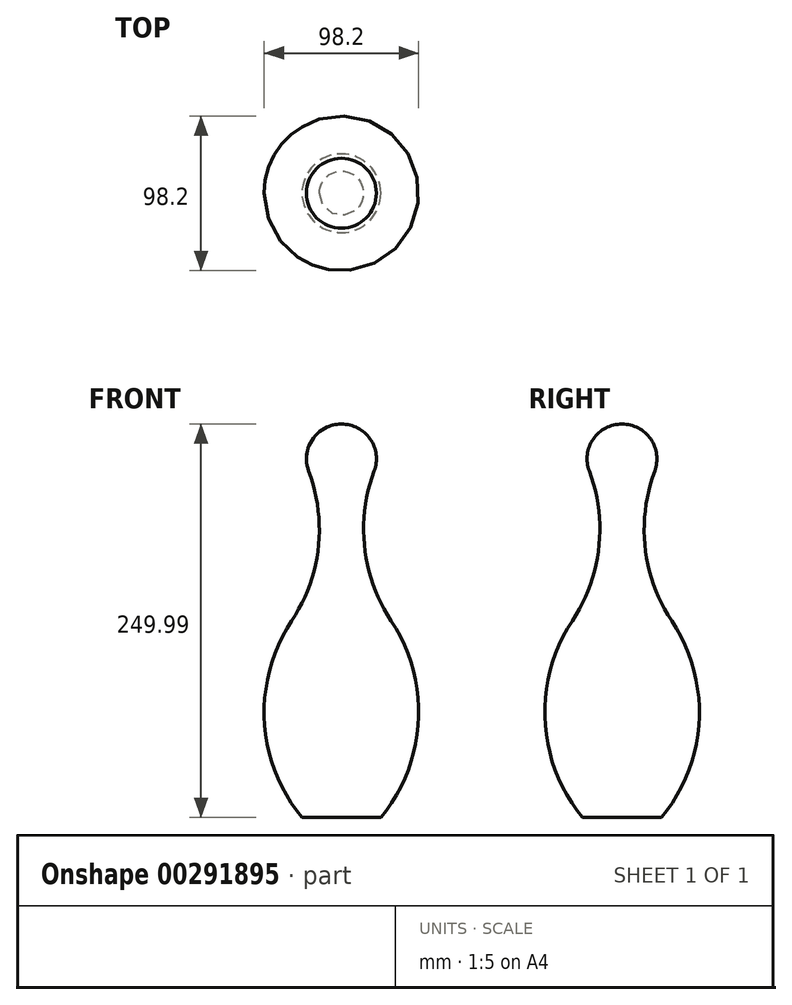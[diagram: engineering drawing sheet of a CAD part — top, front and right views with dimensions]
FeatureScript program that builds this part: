
annotation { "Feature Type Name" : "Feature", "Feature Type Description" : "" }
export const myFeature = defineFeature(function(context is Context, id is Id, definition is map)
    precondition{}
    {
        {
            var Q0;
            Q0=qCreatedBy(makeId("Front.planeOp"),FACE);
            var sketch = newSketch(context, id + "F0", { "sketchPlane" : qUnion([Q0])});
            skLineSegment(sketch, "E0", {"start": v(0, 0) * mm, "end": v(-25, 0) * mm});
            skArc(sketch, "E1", {"start": v(-31.58, 125) * mm, "mid": v(-48.95, 61.41) * mm, "end": v(-25, 0) * mm});
            skArc(sketch, "E2", {"start": v(-31.58, 125) * mm, "mid": v(-14.74, 171.2) * mm, "end": v(-20.77, 220) * mm});
            skArc(sketch, "E3", {"start": v(0, 250) * mm, "mid": v(-18.24, 240.44) * mm, "end": v(-20.77, 220) * mm});
            skLineSegment(sketch, "E4", {"start": v(0, 0) * mm, "end": v(0, 260.5) * mm});
            skSolve(sketch);
        }
        {
            var Q0;
            {var subQ1=sQuery(id+"F0.wireOp",EDGE,"E0");Q0=makeQuery(id+"F0.imprint","IMPRINT",FACE,{"disambiguationData":[TD([[makeQuery(id+"F0.imprint","IMPRINT",EDGE,{"derivedFrom":subQ1}),-1.0]])]});}
            var Q1;
            Q1=sQuery(id+"F0.wireOp",EDGE,"E4");
            revolve(context, id + "F1", {"entities" : qUnion([Q0]), "axis" : qUnion([Q1]), "revolveType" : RevolveType.FULL});
        }
    });
